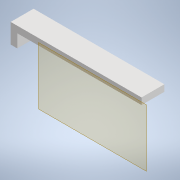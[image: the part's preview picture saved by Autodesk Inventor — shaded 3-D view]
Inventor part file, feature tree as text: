
AUTODESK INVENTOR PART (.ipt)
format: ipt  version: 2020 (Build 240168000, 168)  size: 115,712 bytes
history: native  units: mm
features: other x4, plane x2, sketch x2, extrude x2, direct_edit x1, reference x1, move_body x1
ambient origin geometry x8: Origin, YZ Plane, XZ Plane, XY Plane, X Axis, Y Axis, Z Axis, Center Point
bodies: Solid1 (feature_tree)
feature tree (13):
  plane  "Work Plane1"
  sketch  "Sketch1"  dims[d0=40.0mm d1=2.0mm]
  other  "Work Point1"
  extrude  "Extrusion1"  Depth=2.0mm
  plane  "Work Plane2"
  direct_edit  "Direct Edit1"
  extrude  "Extrusion3"  TaperAngle=0.0deg  [1 undecoded]
  reference  "Reference1"
  sketch  "Sketch3"  dims[d2=10.0mm d3=0.0mm d10=0.0mm d11=0.0mm d12=-0.5mm d19=2.0mm d20=7.0mm d21=7.0mm d22=0.0mm d23=0.0mm]
  parser-record x1  (decoder bookkeeping rows leaked as tree rows — omitted from the tree; the rows remain in map.json)
  other  "motorized.iam"
  other  "funnel:1"
  move_body  "Move1"
note: 1 required parameter value undecoded (feature->parameter linkage not recoverable at this tier; creation-order binding heuristic only, values carry confidence <= 0.55)
note: 1 file-system path scrubbed to <path> (originals preserved in map.json)
